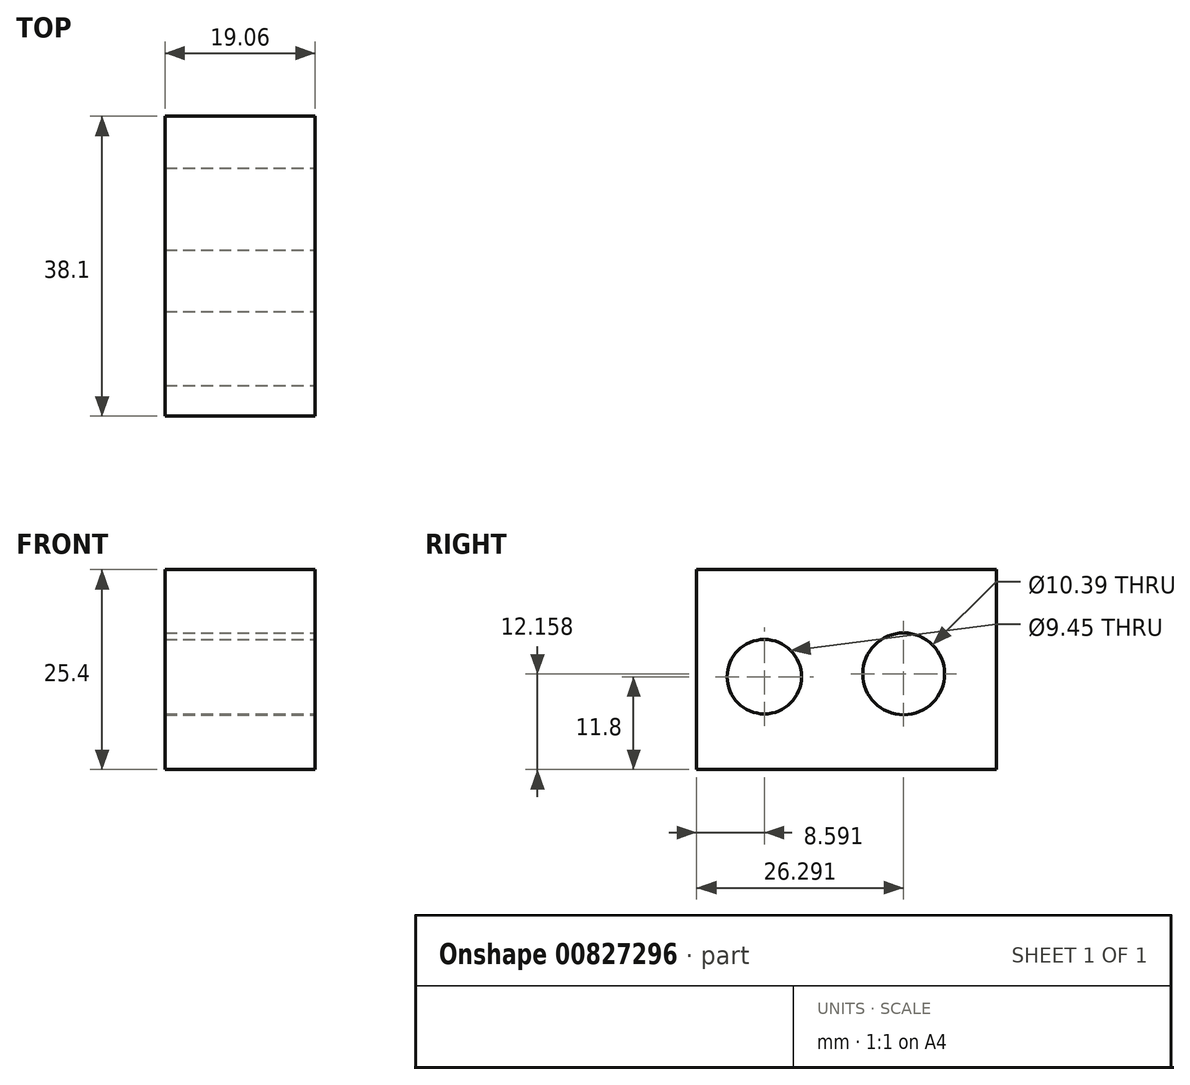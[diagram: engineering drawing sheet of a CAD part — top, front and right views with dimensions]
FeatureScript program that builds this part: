
annotation { "Feature Type Name" : "Feature", "Feature Type Description" : "" }
export const myFeature = defineFeature(function(context is Context, id is Id, definition is map)
    precondition{}
    {
        {
            var Q0;
            Q0=qCreatedBy(makeId("Top.planeOp"),FACE);
            var sketch = newSketch(context, id + "F0", { "sketchPlane" : qUnion([Q0])});
            skLineSegment(sketch, "E0.bottom", {"start": v(-9.52, -19.05) * mm, "end": v(9.53, -19.05) * mm});
            skLineSegment(sketch, "E0.top", {"start": v(-9.53, 19.05) * mm, "end": v(9.52, 19.05) * mm});
            skLineSegment(sketch, "E0.left", {"start": v(-9.52, -19.05) * mm, "end": v(-9.53, 19.05) * mm});
            skLineSegment(sketch, "E0.right", {"start": v(9.53, -19.05) * mm, "end": v(9.52, 19.05) * mm});
            skPoint(sketch, "E0.middle", {"position": v(0, 0) * mm});
            skSolve(sketch);
        }
        {
            var Q0;
            Q0=makeQuery(id+"F0.imprint","IMPRINT",FACE,{"disambiguationData":[TD([[makeQuery(id+"F0.imprint","IMPRINT",EDGE,{"derivedFrom":sQuery(id+"F0.wireOp",EDGE,"E0.bottom")}),1.0]])]});
            extrude(context, id + "F1", {"entities" : qUnion([Q0]), "depth" : 25.4 * mm, "offsetDistance" : 25.4 * mm});
        }
        {
            var Q0;
            Q0=qCreatedBy(makeId("Right.planeOp"),FACE);
            var sketch = newSketch(context, id + "F2", { "sketchPlane" : qUnion([Q0])});
            skCircle(sketch, "E1", {"center": v(-10.46, 11.8) * mm, "radius": 4.72 * mm});
            skCircle(sketch, "E2", {"center": v(7.24, 12.16) * mm, "radius": 5.2 * mm});
            skSolve(sketch);
        }
        {
            var Q0;
            Q0 = qSketchRegion(id + "F2", true);
            extrude(context, id + "F3", {"entities" : qUnion([Q0]), "operationType" : NewBodyOperationType.REMOVE, "oppositeDirection" : true, "depth" : 25.4 * mm, "offsetDistance" : 25.4 * mm, "hasSecondDirection" : true, "secondDirectionOppositeDirection" : false, "secondDirectionDepth" : 25.4 * mm});
        }
    });
